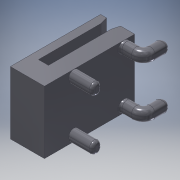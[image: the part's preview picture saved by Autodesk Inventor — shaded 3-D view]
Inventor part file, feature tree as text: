
AUTODESK INVENTOR PART (.ipt)
format: ipt  version: 2016 (Build 200138000, 138)  size: 310,272 bytes
history: native  units: mm
features: sketch x6, extrude x4, fillet x2, chamfer x2, sweep x1, plane x1, pattern_linear x1
ambient origin geometry x8: Origin, YZ Plane, XZ Plane, XY Plane, X Axis, Y Axis, Z Axis, Center Point
bodies: Body1 (feature_tree)
feature tree (17):
  sweep  "Sweep1"
  extrude  "Extrusion2"  Depth=3.5mm
  fillet  "Fillet1"  Radius=4.7mm
  extrude  "Extrusion3"  TaperAngle=0.0deg  [1 undecoded]
  fillet  "Fillet2"  Radius=10.0mm
  plane  "Work Plane1"
  pattern_linear  "Rectangular Pattern1"  Spacing1=1.1mm  [1 undecoded]
  extrude  "Extrusion7"  Depth=10.0mm TaperAngle=0.0deg
  extrude  "Extrusion9"  Depth=10.0mm
  chamfer  "Chamfer1"  Distance=6.108652mm
  chamfer  "Chamfer2"  Distance=2.95mm
  sketch  "Sketch2"  dims[d11=40.0mm d12=11.7mm]
  sketch  "Sketch3"  dims[d13=12.0mm d14=3.5mm d15=4.7mm]
  sketch  "Sketch4"  dims[d16=1.2mm d17=0.0mm d18=0.0mm d19=10.0mm d20=0.0mm]
  sketch  "Sketch5"  dims[d21=1.5mm]
  sketch  "Sketch10"  dims[d22=25.4mm]
  sketch  "Sketch12"  dims[d23=4.7mm d24=1.1mm d25=14.05mm d26=0.0mm d27=1.5mm d60=6.108652mm d61=2.95mm d64=31.3mm d65=0.0mm d73=20.0mm d75=25.4mm d76=45.0mm d77=17.0mm d78=5.0mm d79=4.0mm d80=35.0mm d81=10.0mm d82=0.0mm d83=1.0mm d84=2.0mm d85=75.0deg d86=1.0mm d87=2.0mm d88=75.0deg]
note: 2 required parameter values undecoded (feature->parameter linkage not recoverable at this tier; creation-order binding heuristic only, values carry confidence <= 0.55)
